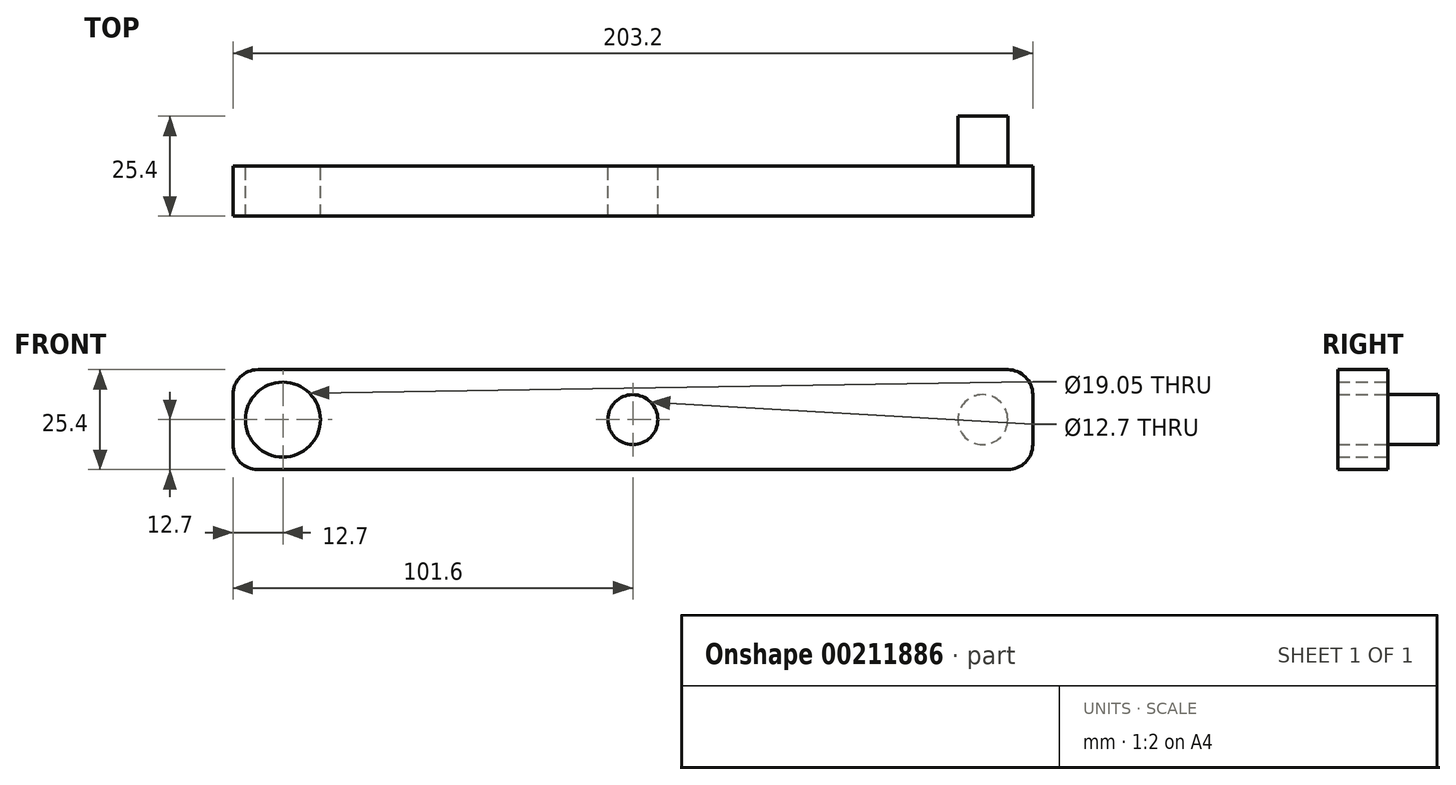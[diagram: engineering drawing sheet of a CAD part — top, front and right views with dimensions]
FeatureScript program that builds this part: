
annotation { "Feature Type Name" : "Feature", "Feature Type Description" : "" }
export const myFeature = defineFeature(function(context is Context, id is Id, definition is map)
    precondition{}
    {
        {
            var Q0;
            Q0=qCreatedBy(makeId("Front.planeOp"),FACE);
            var sketch = newSketch(context, id + "F0", { "sketchPlane" : qUnion([Q0])});
            skLineSegment(sketch, "E0.bottom", {"start": v(95.25, 12.7) * mm, "end": v(-95.25, 12.7) * mm});
            skLineSegment(sketch, "E0.top", {"start": v(95.25, -12.7) * mm, "end": v(-95.25, -12.7) * mm});
            skLineSegment(sketch, "E0.left", {"start": v(101.6, 6.35) * mm, "end": v(101.6, -6.35) * mm});
            skLineSegment(sketch, "E0.right", {"start": v(-101.6, 6.35) * mm, "end": v(-101.6, -6.35) * mm});
            skPoint(sketch, "E0.middle", {"position": v(0, 0) * mm});
            skCircle(sketch, "E1", {"center": v(-88.9, 0) * mm, "radius": 9.53 * mm});
            skCircle(sketch, "E2", {"center": v(0, 0) * mm, "radius": 6.35 * mm});
            skPoint(sketch, "E3.visualSharp", {"position": v(-101.6, 12.7) * mm});
            skArc(sketch, "E3.filletArc", {"start": v(-95.25, 12.7) * mm, "mid": v(-99.74, 10.84) * mm, "end": v(-101.6, 6.35) * mm});
            skPoint(sketch, "E4.visualSharp", {"position": v(-101.6, -12.7) * mm});
            skArc(sketch, "E4.filletArc", {"start": v(-101.6, -6.35) * mm, "mid": v(-99.74, -10.84) * mm, "end": v(-95.25, -12.7) * mm});
            skPoint(sketch, "E5.visualSharp", {"position": v(101.6, 12.7) * mm});
            skArc(sketch, "E5.filletArc", {"start": v(101.6, 6.35) * mm, "mid": v(99.74, 10.84) * mm, "end": v(95.25, 12.7) * mm});
            skPoint(sketch, "E6.visualSharp", {"position": v(101.6, -12.7) * mm});
            skArc(sketch, "E6.filletArc", {"start": v(95.25, -12.7) * mm, "mid": v(99.74, -10.84) * mm, "end": v(101.6, -6.35) * mm});
            skSolve(sketch);
        }
        {
            var Q0;
            Q0=makeQuery(id+"F0.imprint","IMPRINT",FACE,{"disambiguationData":[TD([[makeQuery(id+"F0.imprint","IMPRINT",EDGE,{"derivedFrom":sQuery(id+"F0.wireOp",EDGE,"E0.bottom")}),1.0]])]});
            extrude(context, id + "F1", {"entities" : qUnion([Q0]), "endBound" : BoundingType.SYMMETRIC, "depth" : 12.7 * mm});
        }
        {
            var Q0;
            Q0=makeQuery(id+"F1.opExtrude","CAP_FACE",FACE,{"disambiguationData":[OSD([sQuery(id+"F0.wireOp",EDGE,"E0.bottom"),sQuery(id+"F0.wireOp",EDGE,"E0.top"),sQuery(id+"F0.wireOp",EDGE,"E0.left"),sQuery(id+"F0.wireOp",EDGE,"E0.right"),sQuery(id+"F0.wireOp",EDGE,"E1"),sQuery(id+"F0.wireOp",EDGE,"E2"),sQuery(id+"F0.wireOp",EDGE,"E3.filletArc"),sQuery(id+"F0.wireOp",EDGE,"E4.filletArc"),sQuery(id+"F0.wireOp",EDGE,"E5.filletArc"),sQuery(id+"F0.wireOp",EDGE,"E6.filletArc")])],"isStart":false});
            var sketch = newSketch(context, id + "F2", { "sketchPlane" : qUnion([Q0])});
            skCircle(sketch, "E7", {"center": v(88.9, 0) * mm, "radius": 6.35 * mm});
            skSolve(sketch);
        }
        {
            var Q0;
            Q0 = qSketchRegion(id + "F2", true);
            extrude(context, id + "F3", {"entities" : qUnion([Q0]), "operationType" : NewBodyOperationType.ADD, "oppositeDirection" : true, "depth" : 25.4 * mm});
        }
    });
